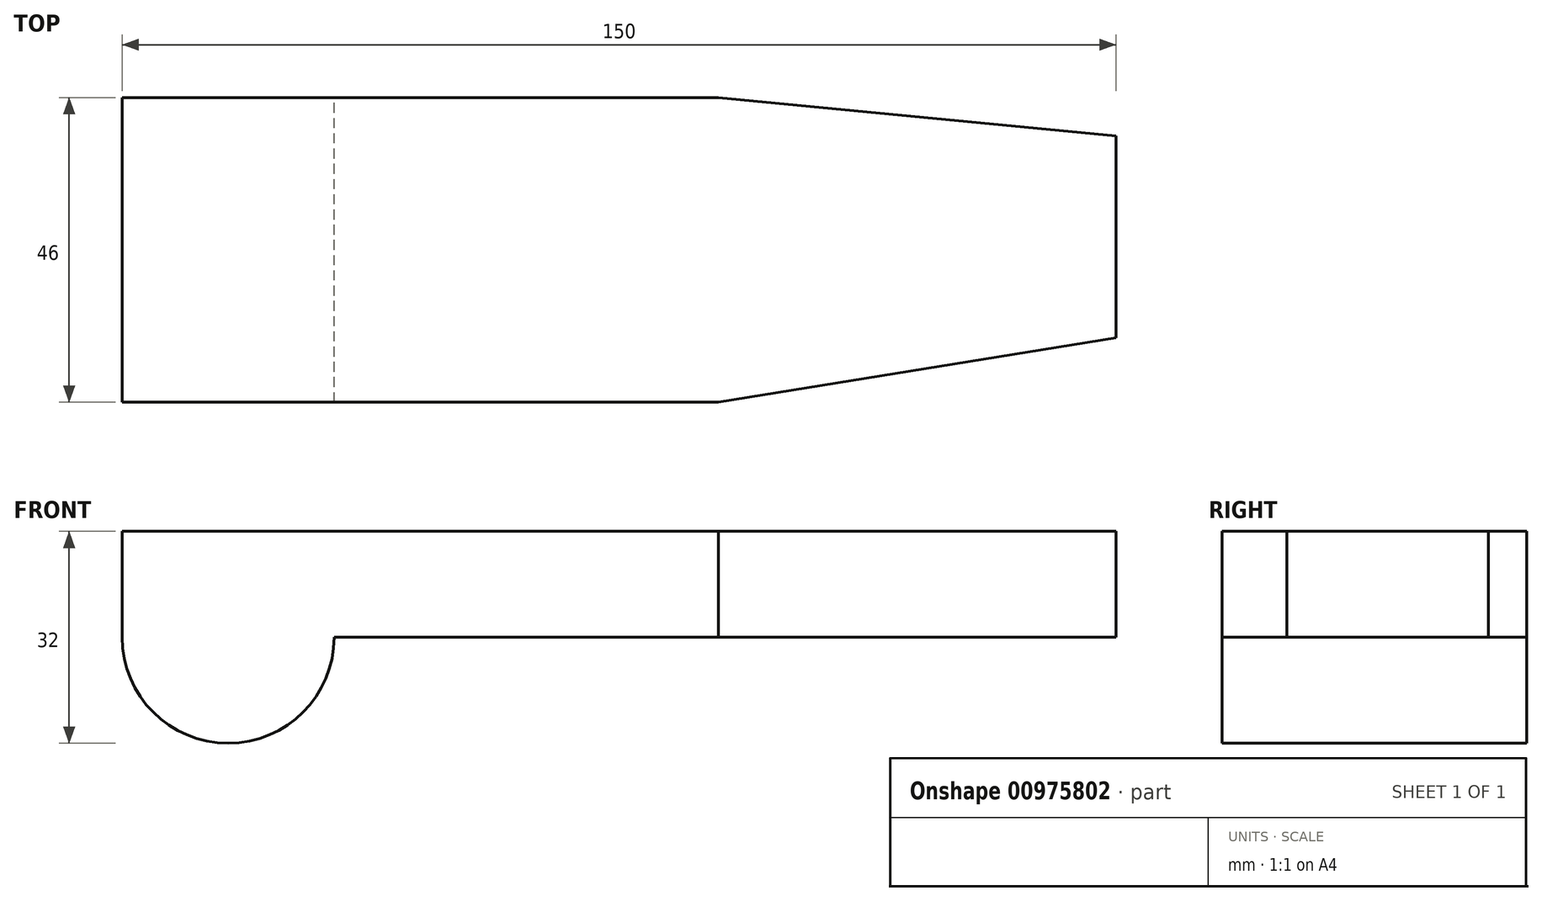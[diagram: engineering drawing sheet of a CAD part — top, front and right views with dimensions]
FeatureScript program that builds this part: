
annotation { "Feature Type Name" : "Feature", "Feature Type Description" : "" }
export const myFeature = defineFeature(function(context is Context, id is Id, definition is map)
    precondition{}
    {
        {
            var Q0;
            Q0=qCreatedBy(makeId("Front.planeOp"),FACE);
            var sketch = newSketch(context, id + "F0", { "sketchPlane" : qUnion([Q0])});
            skArc(sketch, "E0", {"start": v(-16, 0) * mm, "mid": v(0, -16) * mm, "end": v(16, 0) * mm});
            skLineSegment(sketch, "E1.bottom", {"start": v(16, 0) * mm, "end": v(134, 0) * mm});
            skLineSegment(sketch, "E1.top", {"start": v(-16, 16) * mm, "end": v(134, 16) * mm});
            skLineSegment(sketch, "E1.left", {"start": v(-16, 0) * mm, "end": v(-16, 16) * mm});
            skLineSegment(sketch, "E1.right", {"start": v(134, 0) * mm, "end": v(134, 16) * mm});
            skSolve(sketch);
        }
        {
            var Q0;
            Q0=makeQuery(id+"F0.imprint","IMPRINT",FACE,{"disambiguationData":[TD([[makeQuery(id+"F0.imprint","IMPRINT",EDGE,{"derivedFrom":sQuery(id+"F0.wireOp",EDGE,"E0")}),1.0]])]});
            extrude(context, id + "F1", {"entities" : qUnion([Q0]), "depth" : 46 * mm, "offsetDistance" : 25 * mm});
        }
        {
            var Q0;
            Q0 = qSketchRegion(id + "F0", true);
            extrude(context, id + "F2", {"entities" : qUnion([Q0]), "operationType" : NewBodyOperationType.ADD, "depth" : 46 * mm, "offsetDistance" : 25 * mm});
        }
        {
            var Q0;
            Q0=makeQuery(id+"F1.opExtrude","SWEPT_FACE",FACE,{"disambiguationData":[OSD([sQuery(id+"F0.wireOp",EDGE,"E1.top")])]});
            var sketch = newSketch(context, id + "F3", { "sketchPlane" : qUnion([Q0])});
            skLineSegment(sketch, "E2.bottom", {"start": v(-16, 0) * mm, "end": v(52, 0) * mm});
            skLineSegment(sketch, "E2.top", {"start": v(-16, -46) * mm, "end": v(52, -46) * mm});
            skLineSegment(sketch, "E2.left", {"start": v(-16, 0) * mm, "end": v(-16, -46) * mm});
            skLineSegment(sketch, "E2.right", {"start": v(52, 0) * mm, "end": v(52, -46) * mm});
            skLineSegment(sketch, "E3", {"start": v(134, 0) * mm, "end": v(74, 0) * mm});
            skLineSegment(sketch, "E4", {"start": v(74, 0) * mm, "end": v(74, -46) * mm});
            skLineSegment(sketch, "E5", {"start": v(74, -46) * mm, "end": v(134, -46) * mm});
            skLineSegment(sketch, "E6", {"start": v(134, -46) * mm, "end": v(134, 0) * mm});
            skLineSegment(sketch, "E7", {"start": v(74, 0) * mm, "end": v(134, 0) * mm});
            skLineSegment(sketch, "E8", {"start": v(74, 0) * mm, "end": v(134, -5.81) * mm});
            skLineSegment(sketch, "E9", {"start": v(134, -5.81) * mm, "end": v(134, -36.25) * mm});
            skLineSegment(sketch, "E10", {"start": v(134, -36.25) * mm, "end": v(74, -46) * mm});
            skSolve(sketch);
        }
        {
            var Q0;
            {var subQ0=sQuery(id+"F3.wireOp",EDGE,"E5");Q0=makeQuery(id+"F3.imprint","IMPRINT",FACE,{"disambiguationData":[TD([[makeQuery(id+"F3.imprint","IMPRINT",EDGE,{"derivedFrom":subQ0}),1.0]])]});}
            var Q1;
            {var subQ0=sQuery(id+"F3.wireOp",EDGE,"E3");Q1=makeQuery(id+"F3.imprint","IMPRINT",FACE,{"disambiguationData":[TD([[makeQuery(id+"F3.imprint","IMPRINT",EDGE,{"derivedFrom":subQ0}),-1.0]])]});}
            extrude(context, id + "F4", {"entities" : qUnion([Q0, Q1]), "operationType" : NewBodyOperationType.REMOVE, "oppositeDirection" : true, "depth" : 25 * mm, "offsetDistance" : 25 * mm});
        }
    });
